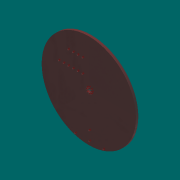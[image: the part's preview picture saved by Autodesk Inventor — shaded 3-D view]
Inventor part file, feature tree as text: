
AUTODESK INVENTOR PART (.ipt)
format: ipt  version: 2013 (Build 170138000, 138)  size: 150,016 bytes
history: native  units: mm
features: sketch x5, extrude x3, hole x2, other x1
ambient origin geometry x8: Origin, YZ Plane, XZ Plane, XY Plane, X Axis, Y Axis, Z Axis, Center Point
feature tree (11):
  other  "ソリッド1"
  extrude  "押し出し1"  Depth=200.0mm
  hole  "穴5"  [1 undecoded]
  extrude  "押し出し4"  Depth=8.0mm
  hole  "穴6"  [1 undecoded]
  extrude  "押し出し7"  Depth=12.0mm
  sketch  "スケッチ1"
  sketch  "スケッチ12"
  sketch  "スケッチ13"
  sketch  "スケッチ14"
  sketch  "スケッチ16"
note: 2 required parameter values undecoded (feature->parameter linkage not recoverable at this tier; creation-order binding heuristic only, values carry confidence <= 0.55)
